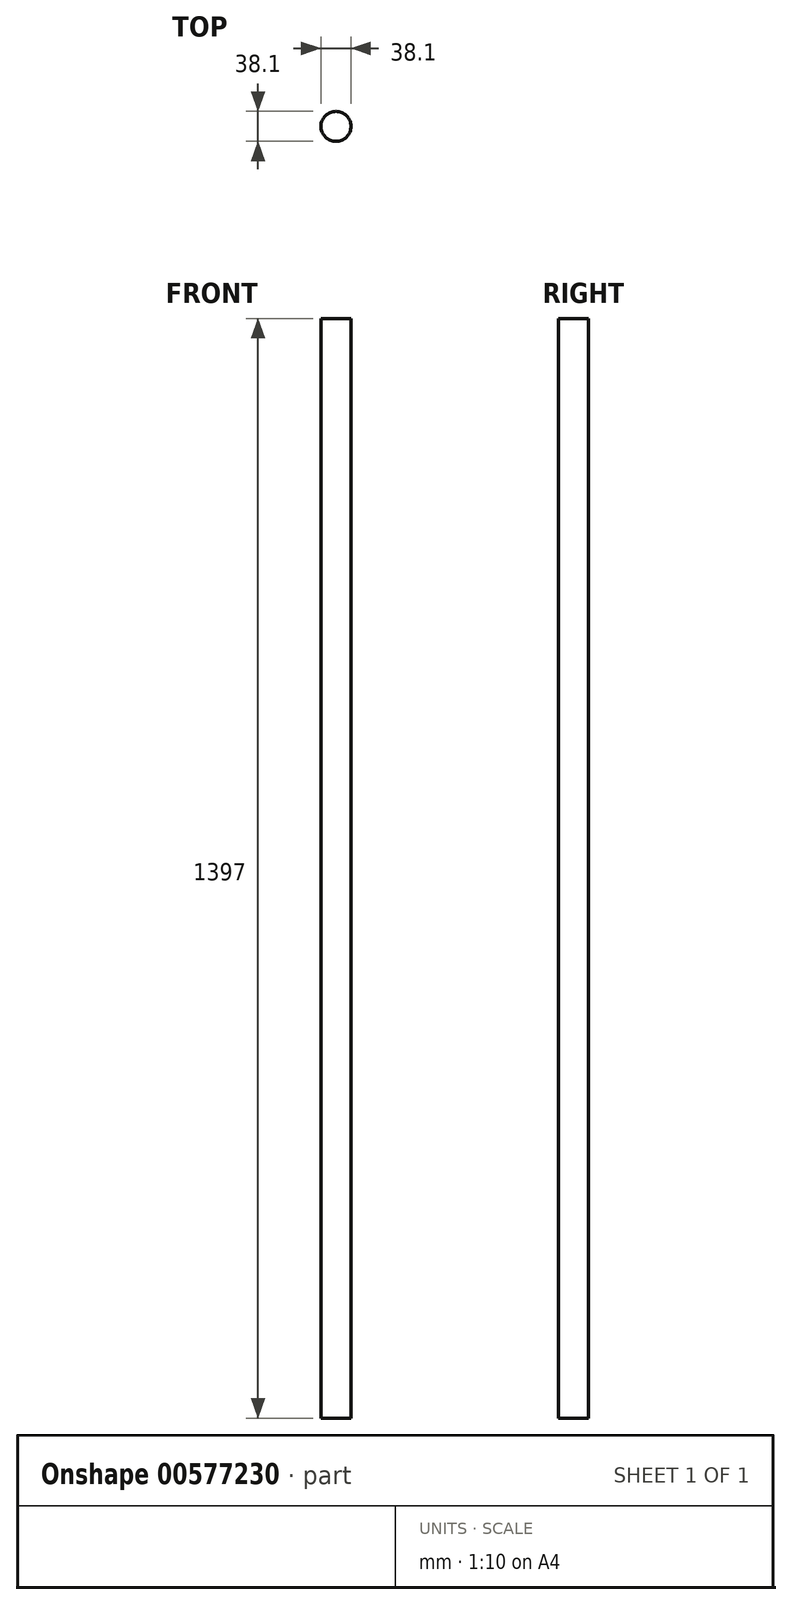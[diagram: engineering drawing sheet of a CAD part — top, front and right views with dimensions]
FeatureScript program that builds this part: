
annotation { "Feature Type Name" : "Feature", "Feature Type Description" : "" }
export const myFeature = defineFeature(function(context is Context, id is Id, definition is map)
    precondition{}
    {
        {
            var Q0;
            Q0=qCreatedBy(makeId("Top.planeOp"),FACE);
            var sketch = newSketch(context, id + "F0", { "sketchPlane" : qUnion([Q0])});
            skCircle(sketch, "E0", {"center": v(-18.31, 0) * mm, "radius": 19.05 * mm});
            skSolve(sketch);
        }
        {
            var Q0;
            Q0 = qSketchRegion(id + "F0", true);
            extrude(context, id + "F1", {"entities" : qUnion([Q0]), "depth" : 1397 * mm, "offsetDistance" : 25.4 * mm});
        }
    });
